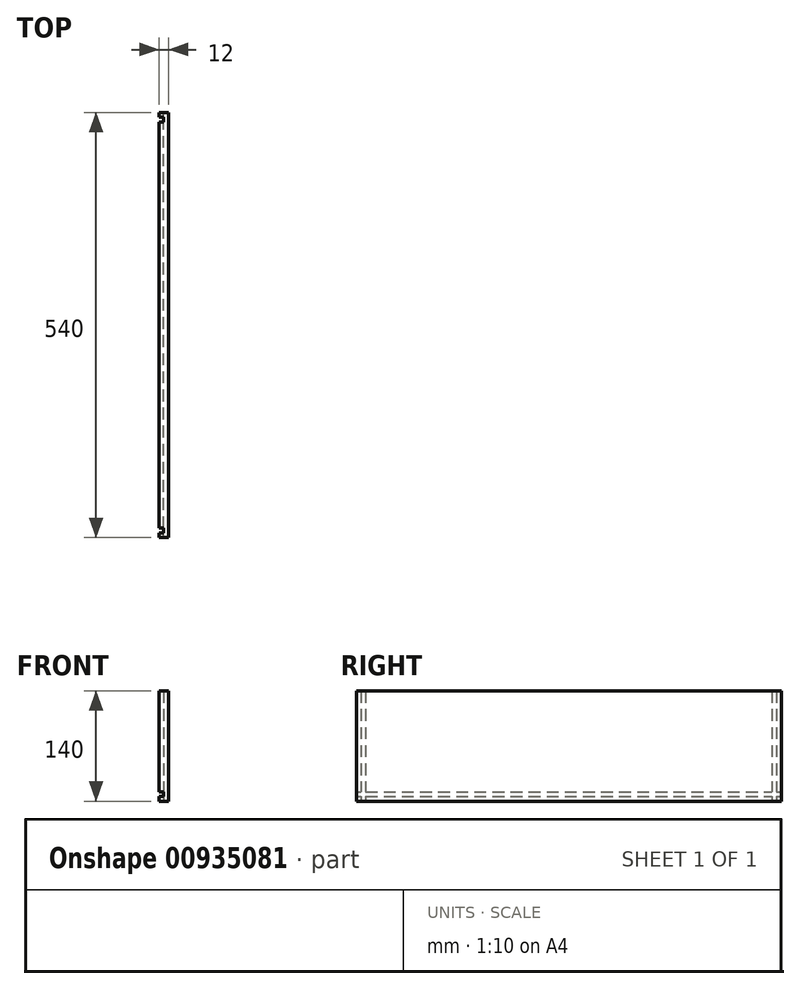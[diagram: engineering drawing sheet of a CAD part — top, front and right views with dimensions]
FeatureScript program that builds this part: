
annotation { "Feature Type Name" : "Feature", "Feature Type Description" : "" }
export const myFeature = defineFeature(function(context is Context, id is Id, definition is map)
    precondition{}
    {
        {
            var Q0;
            Q0=qCreatedBy(makeId("Front.planeOp"),FACE);
            var sketch = newSketch(context, id + "F0", { "sketchPlane" : qUnion([Q0])});
            skLineSegment(sketch, "E0.bottom", {"start": v(0, 0) * mm, "end": v(12, 0) * mm});
            skLineSegment(sketch, "E0.top", {"start": v(0, 140) * mm, "end": v(12, 140) * mm});
            skLineSegment(sketch, "E0.left", {"start": v(0, 0) * mm, "end": v(0, 140) * mm});
            skLineSegment(sketch, "E0.right", {"start": v(12, 0) * mm, "end": v(12, 140) * mm});
            skSolve(sketch);
        }
        {
            var Q0;
            Q0=makeQuery(id+"F0.imprint","IMPRINT",FACE,{"disambiguationData":[TD([[makeQuery(id+"F0.imprint","IMPRINT",EDGE,{"derivedFrom":sQuery(id+"F0.wireOp",EDGE,"E0.bottom")}),1.0]])]});
            extrude(context, id + "F1", {"entities" : qUnion([Q0]), "depth" : 540 * mm, "offsetDistance" : 25 * mm});
        }
        {
            var Q0;
            Q0=qCreatedBy(makeId("Top.planeOp"),FACE);
            var sketch = newSketch(context, id + "F2", { "sketchPlane" : qUnion([Q0])});
            skLineSegment(sketch, "E1.0", {"start": v(0, -540) * mm, "end": v(0, 0) * mm, "construction": true});
            skLineSegment(sketch, "E2.bottom", {"start": v(0, -6) * mm, "end": v(6, -6) * mm});
            skLineSegment(sketch, "E2.top", {"start": v(0, -12) * mm, "end": v(6, -12) * mm});
            skLineSegment(sketch, "E2.left", {"start": v(0, -6) * mm, "end": v(0, -12) * mm});
            skLineSegment(sketch, "E2.right", {"start": v(6, -6) * mm, "end": v(6, -12) * mm});
            skLineSegment(sketch, "E3.bottom", {"start": v(0, -534) * mm, "end": v(6, -534) * mm});
            skLineSegment(sketch, "E3.top", {"start": v(0, -528) * mm, "end": v(6, -528) * mm});
            skLineSegment(sketch, "E3.left", {"start": v(0, -534) * mm, "end": v(0, -528) * mm});
            skLineSegment(sketch, "E3.right", {"start": v(6, -534) * mm, "end": v(6, -528) * mm});
            skSolve(sketch);
        }
        {
            var Q0;
            Q0=qSketchRegion(id+"F2",true);
            extrude(context, id + "F3", {"entities" : qUnion([Q0]), "operationType" : NewBodyOperationType.REMOVE, "endBound" : BoundingType.THROUGH_ALL, "depth" : 25 * mm, "offsetDistance" : 25 * mm});
        }
        {
            var Q0;
            Q0=qCreatedBy(makeId("Front.planeOp"),FACE);
            var sketch = newSketch(context, id + "F4", { "sketchPlane" : qUnion([Q0])});
            skLineSegment(sketch, "E4.bottom", {"start": v(0, 12) * mm, "end": v(6, 12) * mm});
            skLineSegment(sketch, "E4.top", {"start": v(0, 6) * mm, "end": v(6, 6) * mm});
            skLineSegment(sketch, "E4.left", {"start": v(0, 12) * mm, "end": v(0, 6) * mm});
            skLineSegment(sketch, "E4.right", {"start": v(6, 12) * mm, "end": v(6, 6) * mm});
            skSolve(sketch);
        }
        {
            var Q0;
            Q0=qSketchRegion(id+"F4",true);
            extrude(context, id + "F5", {"entities" : qUnion([Q0]), "operationType" : NewBodyOperationType.REMOVE, "endBound" : BoundingType.THROUGH_ALL, "depth" : 25 * mm, "offsetDistance" : 25 * mm});
        }
    });
